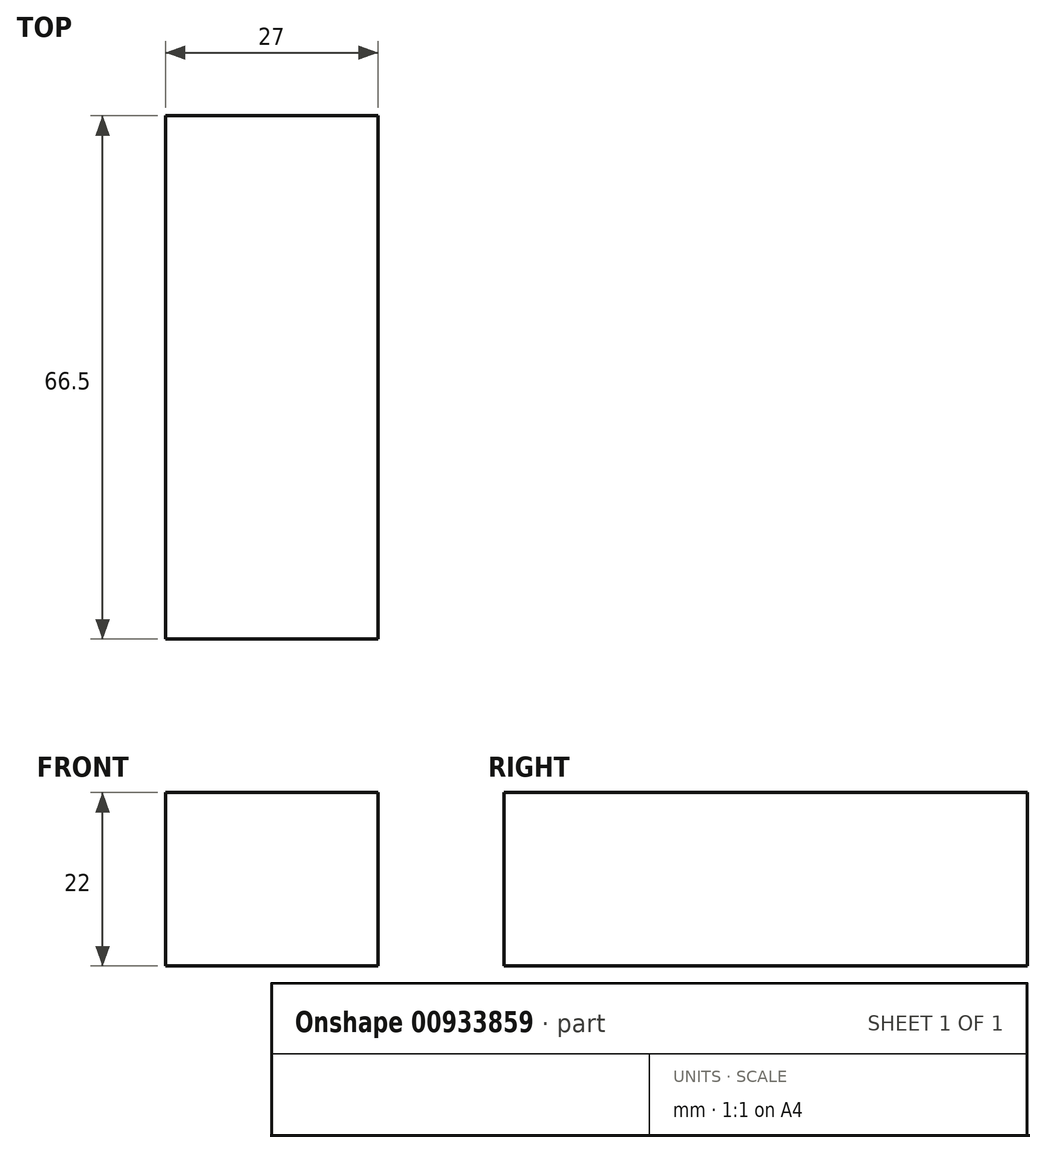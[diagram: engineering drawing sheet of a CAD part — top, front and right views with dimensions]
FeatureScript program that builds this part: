
annotation { "Feature Type Name" : "Feature", "Feature Type Description" : "" }
export const myFeature = defineFeature(function(context is Context, id is Id, definition is map)
    precondition{}
    {
        {
            var Q0;
            Q0=qCreatedBy(makeId("Top.planeOp"),FACE);
            var sketch = newSketch(context, id + "F0", { "sketchPlane" : qUnion([Q0])});
            skLineSegment(sketch, "E0.bottom", {"start": v(-22.5, 38.08) * mm, "end": v(4.5, 38.08) * mm});
            skLineSegment(sketch, "E0.top", {"start": v(-22.5, -28.42) * mm, "end": v(4.5, -28.42) * mm});
            skLineSegment(sketch, "E0.left", {"start": v(-22.5, 38.08) * mm, "end": v(-22.5, -28.42) * mm});
            skLineSegment(sketch, "E0.right", {"start": v(4.5, 38.08) * mm, "end": v(4.5, -28.42) * mm});
            skSolve(sketch);
        }
        {
            var Q0;
            Q0 = qSketchRegion(id + "F0", true);
            extrude(context, id + "F1", {"entities" : qUnion([Q0]), "depth" : 22 * mm, "offsetDistance" : 25 * mm});
        }
        {
            var Q0;
            Q0=makeQuery(id+"F1.opExtrude","SWEPT_BODY",BODY,{"disambiguationData":[OSD([sQuery(id+"F0.wireOp",EDGE,"E0.bottom"),sQuery(id+"F0.wireOp",EDGE,"E0.top"),sQuery(id+"F0.wireOp",EDGE,"E0.left"),sQuery(id+"F0.wireOp",EDGE,"E0.right")])]});
            transform(context, id + "F2", {"entities" : qUnion([Q0]), "transformType" : TransformType.TRANSLATION_3D, "dx" : 0 * mm, "dy" : 0 * mm, "dz" : 7.3 * mm, "makeCopy" : false});
        }
    });
